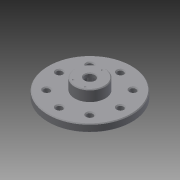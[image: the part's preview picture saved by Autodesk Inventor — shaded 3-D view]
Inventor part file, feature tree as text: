
AUTODESK INVENTOR PART (.ipt)
format: ipt  version: 2016 (Build 200138000, 138)  size: 393,728 bytes
history: native  units: in
note: dims shown in document units (in); Inventor stores cm internally (conversion verified against a paired STEP export)
features: other x3, sketch x2
ambient origin geometry x8: Origin, YZ Plane, XZ Plane, XY Plane, X Axis, Y Axis, Z Axis, Center Point
bodies: Solid1 (feature_tree)
feature tree (5):
  other  "HN07-N101.ipt"
  other  "Solid1::HN07-N101.ipt"
  other  "TaggingFeature1"
  sketch  "Sketch2"  dims[d0=0.3937in]
  sketch  "Sketch3"  dims[d1=0.2244in d8=0.2244in]
